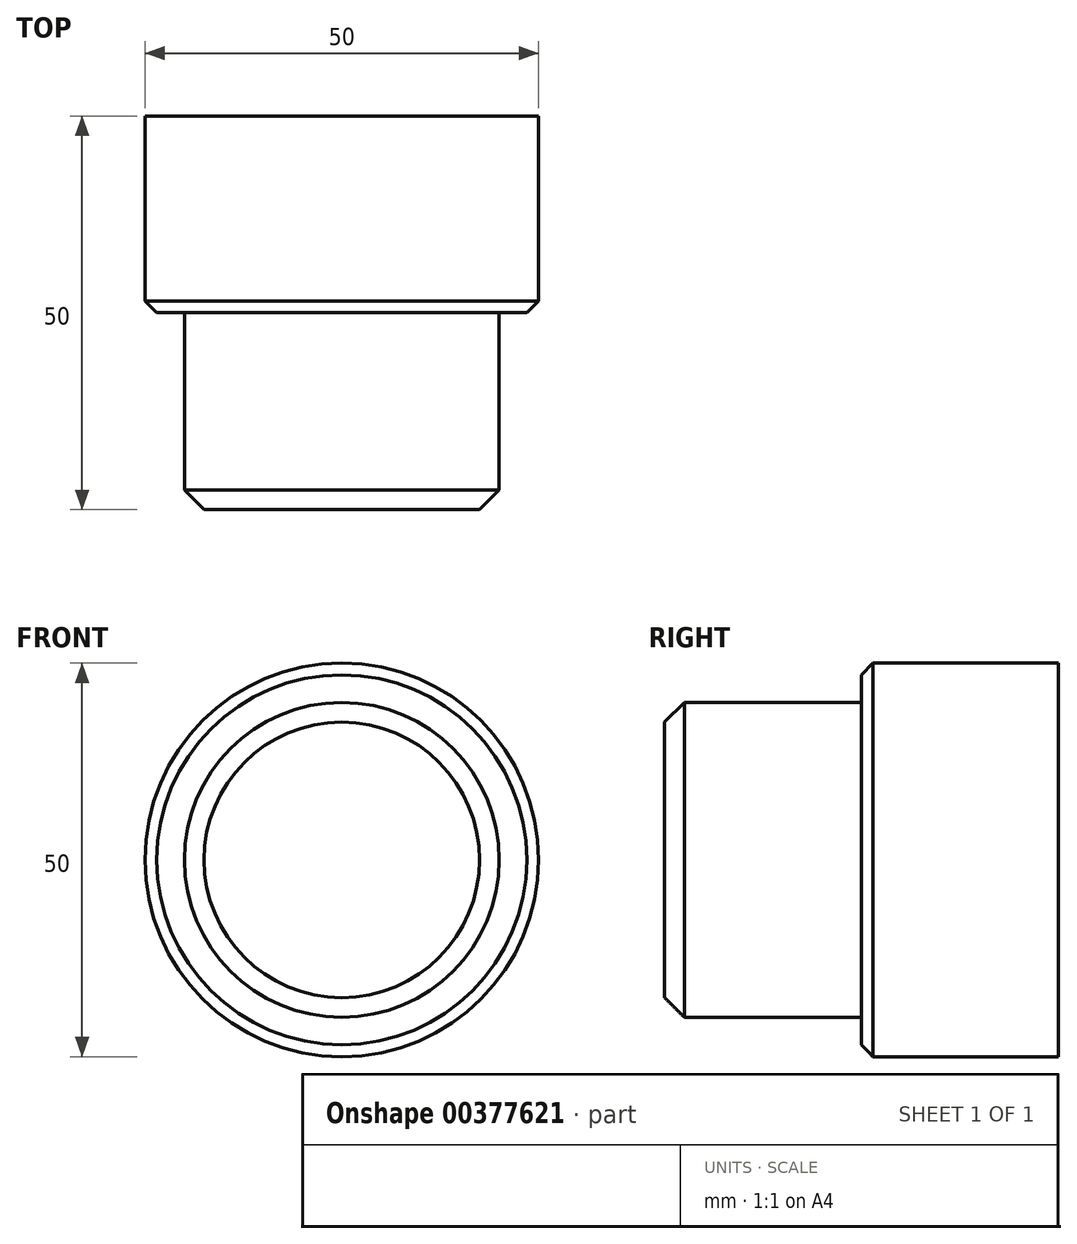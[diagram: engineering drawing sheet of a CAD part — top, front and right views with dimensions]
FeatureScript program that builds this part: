
annotation { "Feature Type Name" : "Feature", "Feature Type Description" : "" }
export const myFeature = defineFeature(function(context is Context, id is Id, definition is map)
    precondition{}
    {
        {
            var Q0;
            Q0=qCreatedBy(makeId("Front.planeOp"),FACE);
            var sketch = newSketch(context, id + "F0", { "sketchPlane" : qUnion([Q0])});
            skCircle(sketch, "E0", {"center": v(0, 0) * mm, "radius": 25 * mm});
            skCircle(sketch, "E1", {"center": v(0, 0) * mm, "radius": 20 * mm});
            skSolve(sketch);
        }
        {
            var Q0;
            Q0=makeQuery(id+"F0.imprint","IMPRINT",FACE,{"disambiguationData":[TD([[makeQuery(id+"F0.imprint","IMPRINT",EDGE,{"derivedFrom":sQuery(id+"F0.wireOp",EDGE,"E1")}),1.0]])]});
            extrude(context, id + "F1", {"entities" : qUnion([Q0]), "depth" : 50 * mm});
        }
        {
            var Q0;
            Q0 = qSketchRegion(id + "F0", true);
            extrude(context, id + "F2", {"entities" : qUnion([Q0]), "operationType" : NewBodyOperationType.ADD, "depth" : 25 * mm});
        }
        {
            var Q0;
            Q0=makeQuery(id+"F1.opExtrude","CAP_FACE",FACE,{"disambiguationData":[OSD([sQuery(id+"F0.wireOp",EDGE,"E1")])],"isStart":false});
            chamfer(context, id + "F3", {"entities" : qUnion([Q0]), "width" : 2.5 * mm, "tangentPropagation" : true});
        }
        {
            var Q0;
            Q0=makeQuery(id+"F2.opExtrude","CAP_EDGE",EDGE,{"disambiguationData":[OSD([sQuery(id+"F0.wireOp",EDGE,"E0")])],"isStart":false});
            chamfer(context, id + "F4", {"entities" : qUnion([Q0]), "width" : 1.5 * mm, "tangentPropagation" : true});
        }
    });
